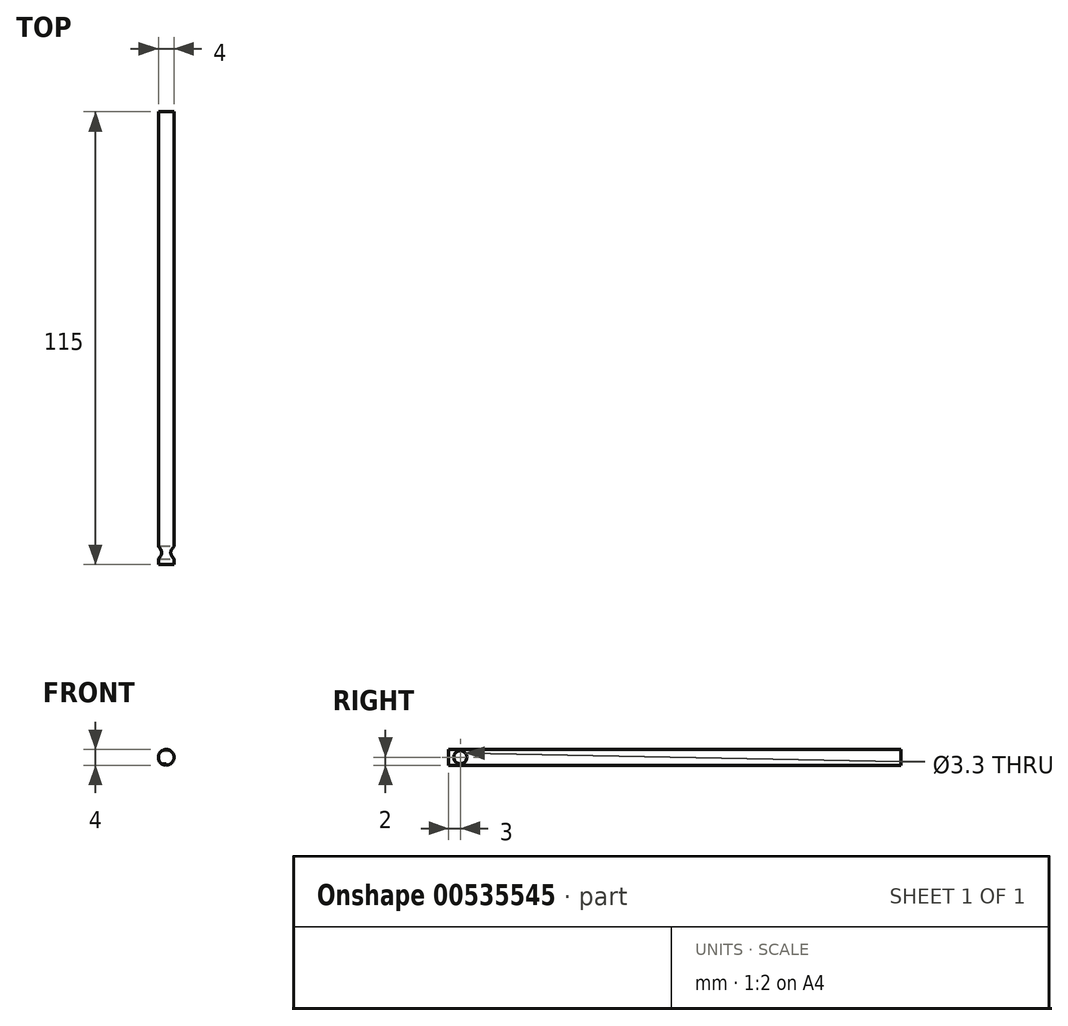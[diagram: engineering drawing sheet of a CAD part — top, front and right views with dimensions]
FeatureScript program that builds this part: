
annotation { "Feature Type Name" : "Feature", "Feature Type Description" : "" }
export const myFeature = defineFeature(function(context is Context, id is Id, definition is map)
    precondition{}
    {
        {
            var Q0;
            Q0=qCreatedBy(makeId("Front.planeOp"),FACE);
            var sketch = newSketch(context, id + "F0", { "sketchPlane" : qUnion([Q0])});
            skCircle(sketch, "E0", {"center": v(0, 0) * mm, "radius": 2 * mm});
            skSolve(sketch);
        }
        {
            var Q0;
            Q0 = qSketchRegion(id + "F0", true);
            extrude(context, id + "F1", {"entities" : qUnion([Q0]), "depth" : 115 * mm, "offsetDistance" : 25 * mm});
        }
        {
            var Q0;
            Q0=qCreatedBy(makeId("Right.planeOp"),FACE);
            var sketch = newSketch(context, id + "F2", { "sketchPlane" : qUnion([Q0])});
            skCircle(sketch, "E1", {"center": v(-112, 0) * mm, "radius": 1.65 * mm});
            skSolve(sketch);
        }
        {
            var Q0;
            Q0 = qSketchRegion(id + "F2", true);
            extrude(context, id + "F3", {"entities" : qUnion([Q0]), "operationType" : NewBodyOperationType.REMOVE, "oppositeDirection" : true, "depth" : 25 * mm, "offsetDistance" : 25 * mm, "symmetric" : true});
        }
    });
